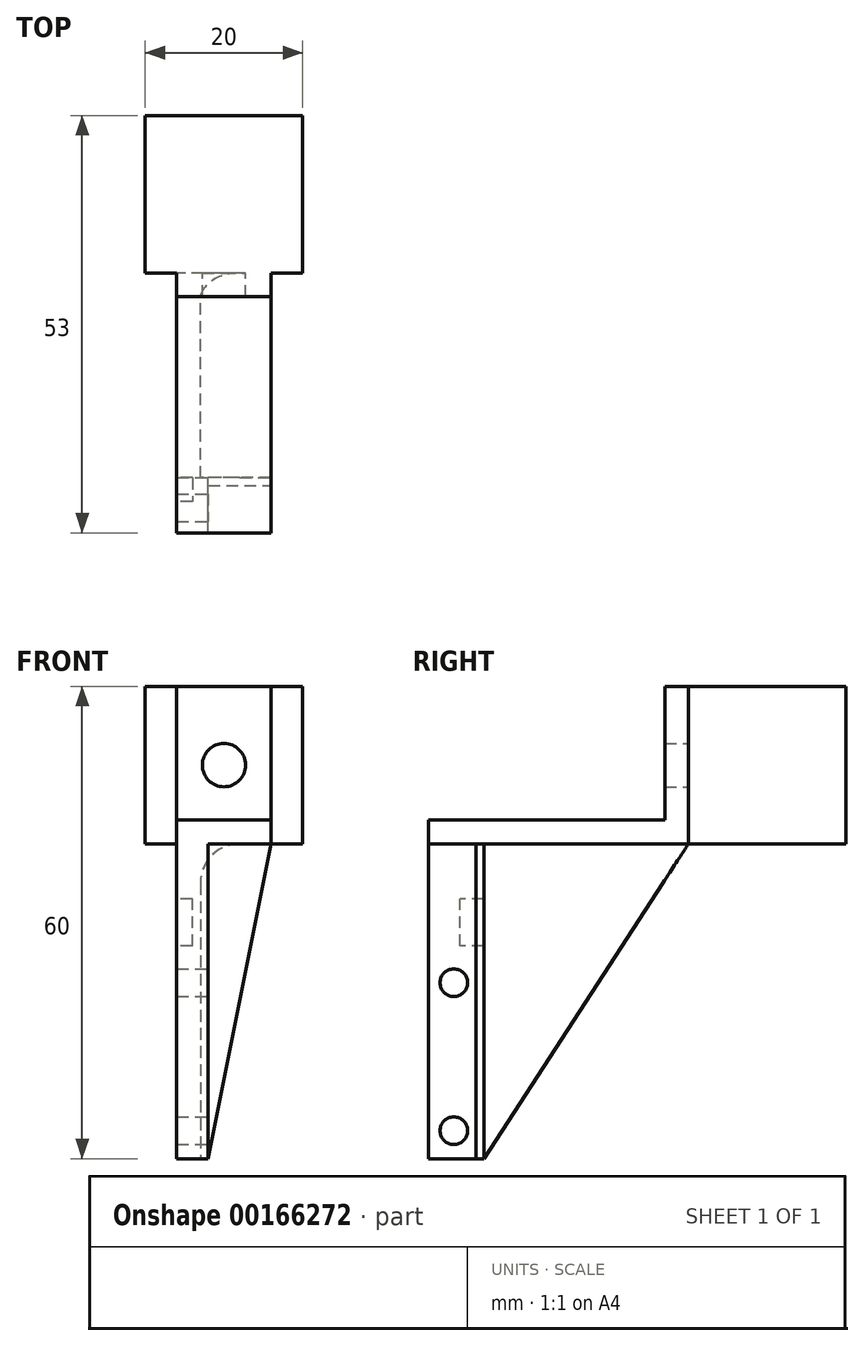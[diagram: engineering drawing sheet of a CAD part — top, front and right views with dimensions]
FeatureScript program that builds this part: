
annotation { "Feature Type Name" : "Feature", "Feature Type Description" : "" }
export const myFeature = defineFeature(function(context is Context, id is Id, definition is map)
    precondition{}
    {
        {
            var Q0;
            Q0=qCreatedBy(makeId("Right.planeOp"),FACE);
            var sketch = newSketch(context, id + "F0", { "sketchPlane" : qUnion([Q0])});
            skLineSegment(sketch, "E0.bottom", {"start": v(10, 10) * mm, "end": v(-10, 10) * mm});
            skLineSegment(sketch, "E0.top", {"start": v(10, -10) * mm, "end": v(-10, -10) * mm});
            skLineSegment(sketch, "E0.left", {"start": v(10, 10) * mm, "end": v(10, -10) * mm});
            skLineSegment(sketch, "E0.right", {"start": v(-10, 10) * mm, "end": v(-10, -10) * mm});
            skPoint(sketch, "E0.middle", {"position": v(0, 0) * mm});
            skSolve(sketch);
        }
        {
            var Q0;
            Q0=makeQuery(id+"F0.imprint","IMPRINT",FACE,{"disambiguationData":[TD([[makeQuery(id+"F0.imprint","IMPRINT",EDGE,{"derivedFrom":sQuery(id+"F0.wireOp",EDGE,"E0.bottom")}),1.0]])]});
            extrude(context, id + "F1", {"entities" : qUnion([Q0]), "depth" : 20 * mm});
        }
        {
            var Q0;
            Q0=makeQuery(id+"F1.opExtrude","SWEPT_FACE",FACE,{"disambiguationData":[OSD([sQuery(id+"F0.wireOp",EDGE,"E0.right")])]});
            var sketch = newSketch(context, id + "F2", { "sketchPlane" : qUnion([Q0])});
            skCircle(sketch, "E1", {"center": v(10, 0) * mm, "radius": 2.75 * mm});
            skPoint(sketch, "E1.centerSnap0", {"position": v(10, 10) * mm});
            skLineSegment(sketch, "E2.bottom", {"start": v(16, -10) * mm, "end": v(4, -10) * mm});
            skLineSegment(sketch, "E2.top", {"start": v(16, 10) * mm, "end": v(4, 10) * mm});
            skLineSegment(sketch, "E2.left", {"start": v(16, -10) * mm, "end": v(16, 10) * mm});
            skLineSegment(sketch, "E2.right", {"start": v(4, -10) * mm, "end": v(4, 10) * mm});
            skSolve(sketch);
        }
        {
            var Q0;
            Q0 = qSketchRegion(id + "F2", true);
            extrude(context, id + "F3", {"entities" : qUnion([Q0]), "depth" : 3 * mm});
        }
        {
            var Q0;
            Q0=makeQuery(id+"F3.opExtrude","CAP_FACE",FACE,{"disambiguationData":[OSD([sQuery(id+"F2.wireOp",EDGE,"E1"),sQuery(id+"F2.wireOp",EDGE,"E2.bottom"),sQuery(id+"F2.wireOp",EDGE,"E2.top"),sQuery(id+"F2.wireOp",EDGE,"E2.left"),sQuery(id+"F2.wireOp",EDGE,"E2.right")])],"isStart":false});
            var sketch = newSketch(context, id + "F4", { "sketchPlane" : qUnion([Q0])});
            skLineSegment(sketch, "E3.bottom", {"start": v(16, -10) * mm, "end": v(4, -10) * mm});
            skLineSegment(sketch, "E3.top", {"start": v(16, -7) * mm, "end": v(4, -7) * mm});
            skLineSegment(sketch, "E3.left", {"start": v(16, -10) * mm, "end": v(16, -7) * mm});
            skLineSegment(sketch, "E3.right", {"start": v(4, -10) * mm, "end": v(4, -7) * mm});
            skSolve(sketch);
        }
        {
            var Q0;
            Q0=makeQuery(id+"F4.imprint","IMPRINT",FACE,{"disambiguationData":[TD([[makeQuery(id+"F4.imprint","IMPRINT",EDGE,{"derivedFrom":sQuery(id+"F4.wireOp",EDGE,"E3.bottom")}),-1.0]])]});
            extrude(context, id + "F5", {"entities" : qUnion([Q0]), "operationType" : NewBodyOperationType.ADD, "offsetDistance" : 25 * mm, "depth" : 30 * mm});
        }
        {
            var Q0;
            Q0=makeQuery(id+"F5.boolean.opBoolean","MERGE",FACE,{"derivedFrom":[makeQuery(id+"F3.opExtrude","SWEPT_FACE",FACE,{"disambiguationData":[OSD([sQuery(id+"F2.wireOp",EDGE,"E2.bottom")])]}),makeQuery(id+"F5.opExtrude","SWEPT_FACE",FACE,{"disambiguationData":[OSD([sQuery(id+"F4.wireOp",EDGE,"E3.bottom")])]})]});
            var sketch = newSketch(context, id + "F6", { "sketchPlane" : qUnion([Q0])});
            skLineSegment(sketch, "E4.bottom", {"start": v(4, 43) * mm, "end": v(8, 43) * mm});
            skLineSegment(sketch, "E4.top", {"start": v(4, 36) * mm, "end": v(8, 36) * mm});
            skLineSegment(sketch, "E4.left", {"start": v(4, 43) * mm, "end": v(4, 36) * mm});
            skLineSegment(sketch, "E4.right", {"start": v(8, 43) * mm, "end": v(8, 36) * mm});
            skSolve(sketch);
        }
        {
            var Q0;
            Q0=makeQuery(id+"F6.imprint","IMPRINT",FACE,{"disambiguationData":[TD([[makeQuery(id+"F6.imprint","IMPRINT",EDGE,{"derivedFrom":sQuery(id+"F6.wireOp",EDGE,"E4.bottom")}),1.0]])]});
            extrude(context, id + "F7", {"entities" : qUnion([Q0]), "operationType" : NewBodyOperationType.ADD, "depth" : 40 * mm});
        }
        {
            var Q0;
            Q0=makeQuery(id+"F7.opExtrude","SWEPT_FACE",FACE,{"disambiguationData":[OSD([sQuery(id+"F6.wireOp",EDGE,"E4.right")])]});
            var sketch = newSketch(context, id + "F8", { "sketchPlane" : qUnion([Q0])});
            skLineSegment(sketch, "E5", {"start": v(-39.8, -50) * mm, "end": v(-39.8, -10) * mm, "construction": true});
            skCircle(sketch, "E6", {"center": v(-39.8, -46.45) * mm, "radius": 1.75 * mm});
            skCircle(sketch, "E7", {"center": v(-39.8, -27.65) * mm, "radius": 1.75 * mm});
            skSolve(sketch);
        }
        {
            var Q0;
            Q0 = qSketchRegion(id + "F8", true);
            extrude(context, id + "F9", {"entities" : qUnion([Q0]), "operationType" : NewBodyOperationType.REMOVE, "oppositeDirection" : true, "depth" : 25 * mm});
        }
        {
            var Q0;
            Q0=makeQuery(id+"F7.opExtrude","SWEPT_FACE",FACE,{"disambiguationData":[OSD([sQuery(id+"F6.wireOp",EDGE,"E4.top")])]});
            var sketch = newSketch(context, id + "F10", { "sketchPlane" : qUnion([Q0])});
            skLineSegment(sketch, "E8", {"start": v(-8, -50) * mm, "end": v(-8, -10) * mm});
            skLineSegment(sketch, "E9", {"start": v(-8, -10) * mm, "end": v(-16, -10) * mm});
            skLineSegment(sketch, "E10", {"start": v(-16, -10) * mm, "end": v(-8, -50) * mm});
            skSolve(sketch);
        }
        {
            var Q0;
            Q0=makeQuery(id+"F10.imprint","IMPRINT",FACE,{"disambiguationData":[TD([[makeQuery(id+"F10.imprint","IMPRINT",EDGE,{"derivedFrom":sQuery(id+"F10.wireOp",EDGE,"E8")}),1.0]])]});
            extrude(context, id + "F11", {"entities" : qUnion([Q0]), "operationType" : NewBodyOperationType.ADD, "oppositeDirection" : true, "depth" : 1 * mm});
        }
        {
            var Q0;
            Q0=makeQuery(id+"F7.boolean.opBoolean","MERGE",FACE,{"derivedFrom":[makeQuery(id+"F5.boolean.opBoolean","MERGE",FACE,{"derivedFrom":[makeQuery(id+"F3.opExtrude","SWEPT_FACE",FACE,{"disambiguationData":[OSD([sQuery(id+"F2.wireOp",EDGE,"E2.right")])]}),makeQuery(id+"F5.opExtrude","SWEPT_FACE",FACE,{"disambiguationData":[OSD([sQuery(id+"F4.wireOp",EDGE,"E3.right")])]})]}),makeQuery(id+"F7.opExtrude","SWEPT_FACE",FACE,{"disambiguationData":[OSD([sQuery(id+"F6.wireOp",EDGE,"E4.left")])]})]});
            var sketch = newSketch(context, id + "F12", { "sketchPlane" : qUnion([Q0])});
            skLineSegment(sketch, "E11.bottom", {"start": v(36, -23) * mm, "end": v(39, -23) * mm});
            skLineSegment(sketch, "E11.top", {"start": v(36, -17) * mm, "end": v(39, -17) * mm});
            skLineSegment(sketch, "E11.left", {"start": v(36, -23) * mm, "end": v(36, -17) * mm});
            skLineSegment(sketch, "E11.right", {"start": v(39, -23) * mm, "end": v(39, -17) * mm});
            skSolve(sketch);
        }
        {
            var Q0;
            Q0=makeQuery(id+"F12.imprint","IMPRINT",FACE,{"disambiguationData":[TD([[makeQuery(id+"F12.imprint","IMPRINT",EDGE,{"derivedFrom":sQuery(id+"F12.wireOp",EDGE,"E11.bottom")}),1.0]])]});
            extrude(context, id + "F13", {"entities" : qUnion([Q0]), "operationType" : NewBodyOperationType.REMOVE, "oppositeDirection" : true, "depth" : 2 * mm});
        }
        {
            var Q0;
            Q0=makeQuery(id+"F7.boolean.opBoolean","MERGE",FACE,{"derivedFrom":[makeQuery(id+"F5.boolean.opBoolean","MERGE",FACE,{"derivedFrom":[makeQuery(id+"F3.opExtrude","SWEPT_FACE",FACE,{"disambiguationData":[OSD([sQuery(id+"F2.wireOp",EDGE,"E2.right")])]}),makeQuery(id+"F5.opExtrude","SWEPT_FACE",FACE,{"disambiguationData":[OSD([sQuery(id+"F4.wireOp",EDGE,"E3.right")])]})]}),makeQuery(id+"F7.opExtrude","SWEPT_FACE",FACE,{"disambiguationData":[OSD([sQuery(id+"F6.wireOp",EDGE,"E4.left")])]})]});
            var sketch = newSketch(context, id + "F14", { "sketchPlane" : qUnion([Q0])});
            skLineSegment(sketch, "E12", {"start": v(36, -10) * mm, "end": v(36, -50) * mm});
            skLineSegment(sketch, "E13", {"start": v(36, -50) * mm, "end": v(10, -10) * mm});
            skSolve(sketch);
        }
        {
            var Q0;
            {var subQ0=sQuery(id+"F14.wireOp",EDGE,"E13");Q0=makeQuery(id+"F14.imprint","IMPRINT",FACE,{"disambiguationData":[TD([[makeQuery(id+"F14.imprint","IMPRINT",EDGE,{"derivedFrom":subQ0}),-1.0]])]});}
            extrude(context, id + "F15", {"entities" : qUnion([Q0]), "operationType" : NewBodyOperationType.ADD, "oppositeDirection" : true, "depth" : 3 * mm});
        }
        {
            var Q0;
            Q0=makeQuery(id+"F15.opExtrude","CAP_EDGE",EDGE,{"disambiguationData":[OSD([sQuery(id+"F0.wireOp",EDGE,"E0.top"),sQuery(id+"F0.wireOp",EDGE,"E0.right"),sQuery(id+"F2.wireOp",EDGE,"E2.bottom"),sQuery(id+"F2.wireOp",EDGE,"E2.right"),sQuery(id+"F4.wireOp",EDGE,"E3.bottom"),sQuery(id+"F4.wireOp",EDGE,"E3.right")])],"isStart":false});
            var Q1;
            Q1=makeQuery(id+"F11.boolean.opBoolean","MERGE",EDGE,{"derivedFrom":[makeQuery(id+"F7.opExtrude","CAP_EDGE",EDGE,{"disambiguationData":[OSD([sQuery(id+"F6.wireOp",EDGE,"E4.top")])],"isStart":true}),makeQuery(id+"F11.opExtrude","CAP_EDGE",EDGE,{"disambiguationData":[OSD([sQuery(id+"F10.wireOp",EDGE,"E9")])],"isStart":true})]});
            var Q2;
            Q2=makeQuery(id+"F15.opExtrude","CAP_EDGE",EDGE,{"disambiguationData":[OSD([sQuery(id+"F14.wireOp",EDGE,"E12")])],"isStart":false});
            fillet(context, id + "F16", {"entities" : qUnion([Q0, Q1, Q2]), "radius" : 5 * mm, "tangentPropagation" : true, "allowEdgeOverflow" : false});
        }
    });
